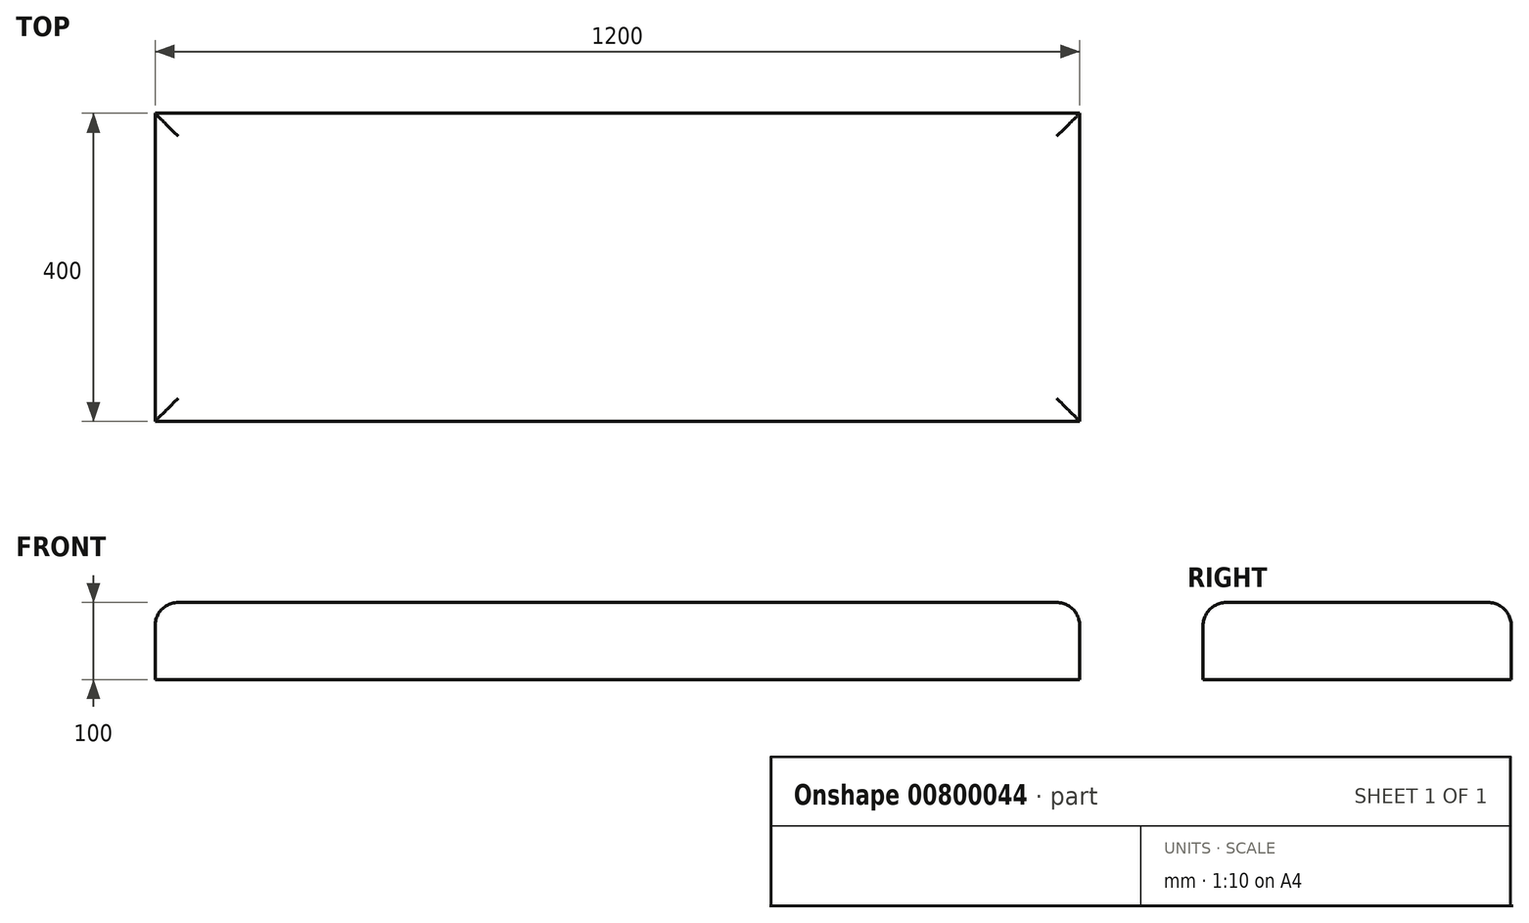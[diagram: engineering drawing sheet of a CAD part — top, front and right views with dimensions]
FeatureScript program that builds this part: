
annotation { "Feature Type Name" : "Feature", "Feature Type Description" : "" }
export const myFeature = defineFeature(function(context is Context, id is Id, definition is map)
    precondition{}
    {
        {
            var Q0;
            Q0=qCreatedBy(makeId("Top.planeOp"),FACE);
            var sketch = newSketch(context, id + "F0", { "sketchPlane" : qUnion([Q0])});
            skLineSegment(sketch, "E0.bottom", {"start": v(600, -200) * mm, "end": v(-600, -200) * mm});
            skLineSegment(sketch, "E0.top", {"start": v(600, 200) * mm, "end": v(-600, 200) * mm});
            skLineSegment(sketch, "E0.left", {"start": v(600, -200) * mm, "end": v(600, 200) * mm});
            skLineSegment(sketch, "E0.right", {"start": v(-600, -200) * mm, "end": v(-600, 200) * mm});
            skPoint(sketch, "E0.middle", {"position": v(0, 0) * mm});
            skSolve(sketch);
        }
        {
            var Q0;
            Q0 = qSketchRegion(id + "F0", true);
            extrude(context, id + "F1", {"entities" : qUnion([Q0]), "depth" : 100 * mm, "offsetDistance" : 25 * mm});
        }
        {
            var Q0;
            Q0=makeQuery(id+"F1.opExtrude","CAP_EDGE",EDGE,{"disambiguationData":[OSD([sQuery(id+"F0.wireOp",EDGE,"E0.top")])],"isStart":false});
            var Q1;
            Q1=makeQuery(id+"F1.opExtrude","CAP_EDGE",EDGE,{"disambiguationData":[OSD([sQuery(id+"F0.wireOp",EDGE,"E0.left")])],"isStart":false});
            var Q2;
            Q2=makeQuery(id+"F1.opExtrude","CAP_EDGE",EDGE,{"disambiguationData":[OSD([sQuery(id+"F0.wireOp",EDGE,"E0.bottom")])],"isStart":false});
            var Q3;
            Q3=makeQuery(id+"F1.opExtrude","CAP_EDGE",EDGE,{"disambiguationData":[OSD([sQuery(id+"F0.wireOp",EDGE,"E0.right")])],"isStart":false});
            fillet(context, id + "F2", {"entities" : qUnion([Q0, Q1, Q2, Q3]), "radius" : 30 * mm, "tangentPropagation" : true, "allowEdgeOverflow" : false});
        }
    });
